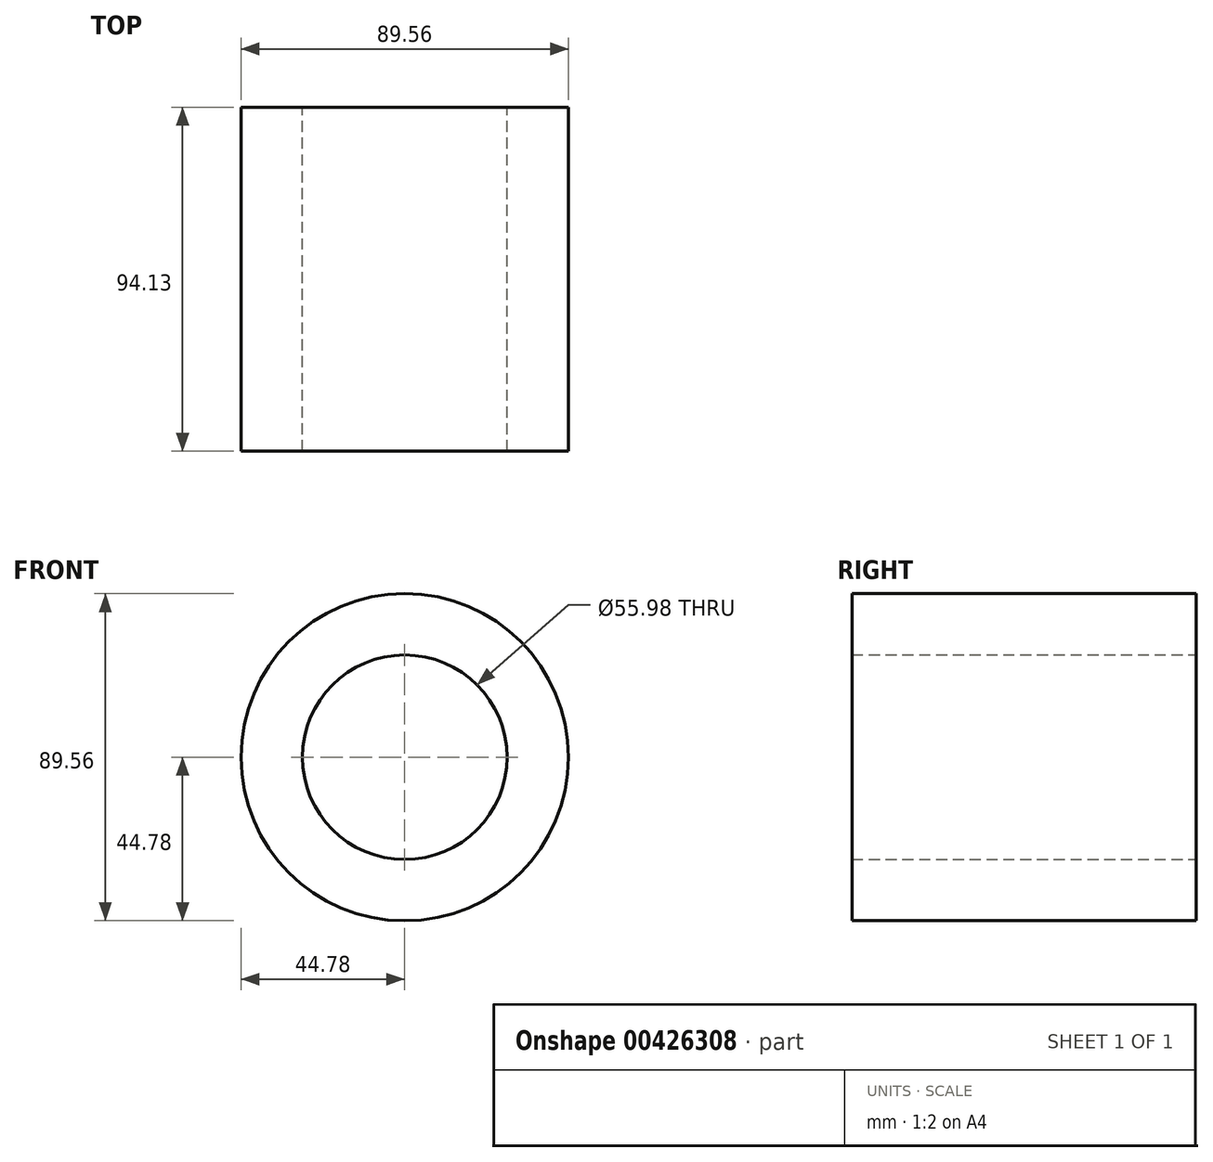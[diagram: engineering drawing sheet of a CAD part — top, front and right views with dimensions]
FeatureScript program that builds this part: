
annotation { "Feature Type Name" : "Feature", "Feature Type Description" : "" }
export const myFeature = defineFeature(function(context is Context, id is Id, definition is map)
    precondition{}
    {
        {
            var Q0;
            Q0=qCreatedBy(makeId("Front.planeOp"),FACE);
            var sketch = newSketch(context, id + "F0", { "sketchPlane" : qUnion([Q0])});
            skCircle(sketch, "E0", {"center": v(0, 0) * mm, "radius": 44.78 * mm});
            skCircle(sketch, "E1", {"center": v(0, 0) * mm, "radius": 27.99 * mm});
            skSolve(sketch);
        }
        {
            var Q0;
            Q0=makeQuery(id+"F0.imprint","IMPRINT",FACE,{"disambiguationData":[TD([[makeQuery(id+"F0.imprint","IMPRINT",EDGE,{"derivedFrom":sQuery(id+"F0.wireOp",EDGE,"E0")}),1.0]])]});
            extrude(context, id + "F1", {"entities" : qUnion([Q0]), "depth" : 94.13 * mm});
        }
    });
